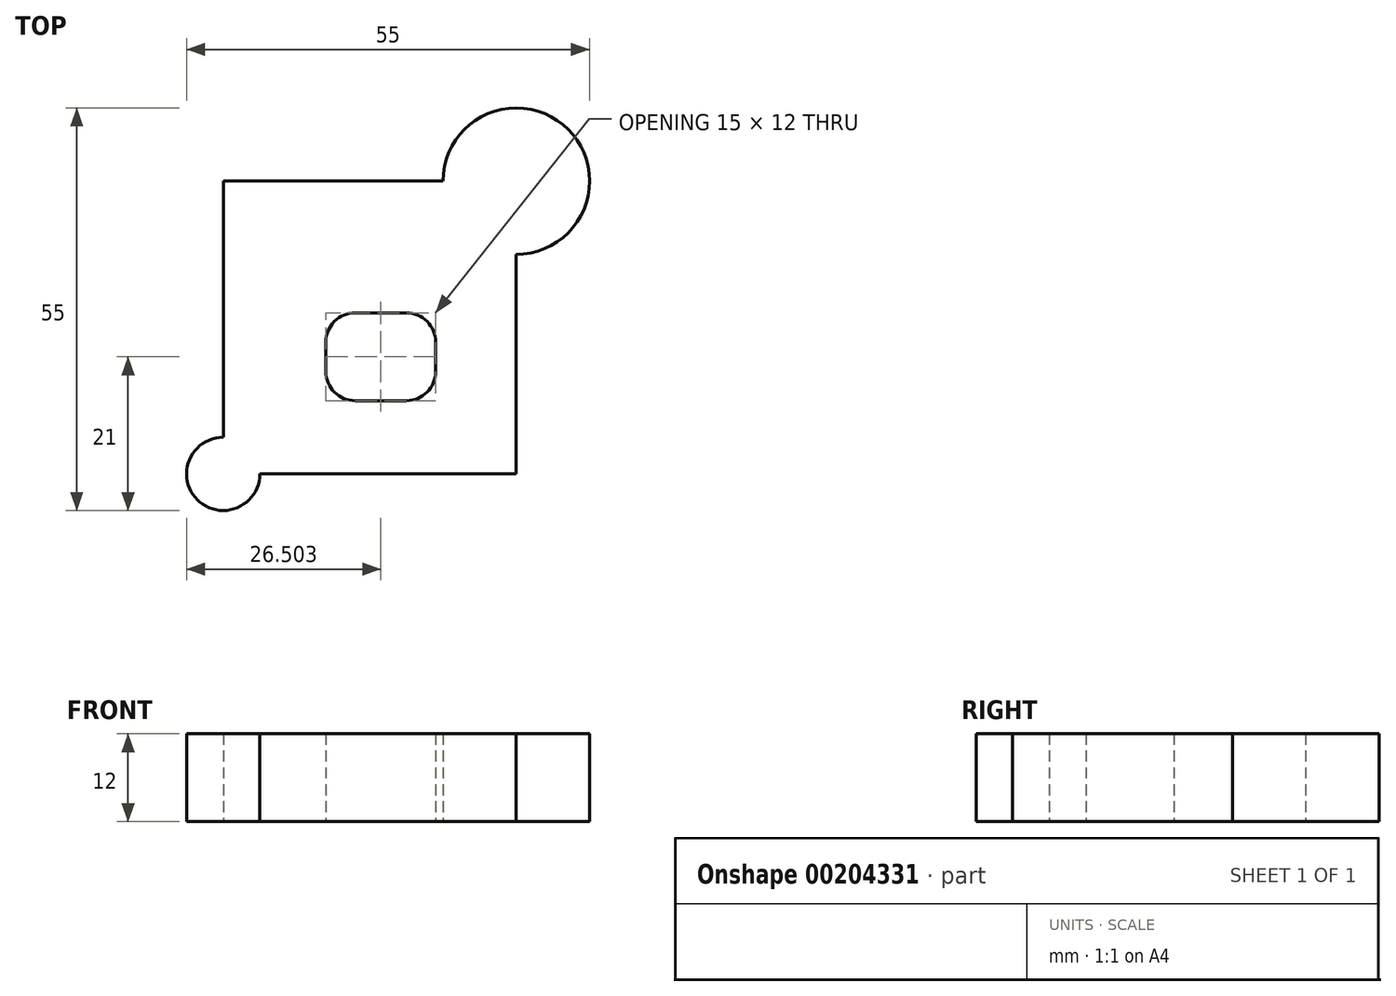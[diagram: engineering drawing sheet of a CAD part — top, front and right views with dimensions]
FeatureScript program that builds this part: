
annotation { "Feature Type Name" : "Feature", "Feature Type Description" : "" }
export const myFeature = defineFeature(function(context is Context, id is Id, definition is map)
    precondition{}
    {
        {
            var Q0;
            Q0=qCreatedBy(makeId("Top.planeOp"),FACE);
            var sketch = newSketch(context, id + "F0", { "sketchPlane" : qUnion([Q0])});
            skLineSegment(sketch, "E0.bottom", {"start": v(-39.87, 40) * mm, "end": v(0.13, 40) * mm});
            skLineSegment(sketch, "E0.top", {"start": v(-39.87, 0) * mm, "end": v(0.13, 0) * mm});
            skLineSegment(sketch, "E0.left", {"start": v(-39.87, 40) * mm, "end": v(-39.87, 0) * mm});
            skLineSegment(sketch, "E0.right", {"start": v(0.13, 40) * mm, "end": v(0.13, 0) * mm});
            skCircle(sketch, "E1", {"center": v(0.13, 40) * mm, "radius": 10 * mm});
            skCircle(sketch, "E2", {"center": v(-39.87, 0) * mm, "radius": 5 * mm});
            skLineSegment(sketch, "E3.bottom", {"start": v(-21.87, 22) * mm, "end": v(-14.87, 22) * mm});
            skLineSegment(sketch, "E3.top", {"start": v(-21.87, 10) * mm, "end": v(-14.87, 10) * mm});
            skLineSegment(sketch, "E3.left", {"start": v(-25.87, 18) * mm, "end": v(-25.87, 14) * mm});
            skLineSegment(sketch, "E3.right", {"start": v(-10.87, 18) * mm, "end": v(-10.87, 14) * mm});
            skPoint(sketch, "E4.visualSharp", {"position": v(-25.87, 22) * mm});
            skArc(sketch, "E4.filletArc", {"start": v(-21.87, 22) * mm, "mid": v(-24.7, 20.83) * mm, "end": v(-25.87, 18) * mm});
            skPoint(sketch, "E5.visualSharp", {"position": v(-10.87, 22) * mm});
            skArc(sketch, "E5.filletArc", {"start": v(-10.87, 18) * mm, "mid": v(-12.04, 20.83) * mm, "end": v(-14.87, 22) * mm});
            skPoint(sketch, "E6.visualSharp", {"position": v(-10.87, 10) * mm});
            skArc(sketch, "E6.filletArc", {"start": v(-14.87, 10) * mm, "mid": v(-12.04, 11.17) * mm, "end": v(-10.87, 14) * mm});
            skPoint(sketch, "E7.visualSharp", {"position": v(-25.87, 10) * mm});
            skArc(sketch, "E7.filletArc", {"start": v(-25.87, 14) * mm, "mid": v(-24.7, 11.17) * mm, "end": v(-21.87, 10) * mm});
            skSolve(sketch);
        }
        {
            var Q0;
            Q0=makeQuery(id+"F0.imprint","IMPRINT",FACE,{"disambiguationData":[TD([[makeQuery(id+"F0.imprint","IMPRINT",EDGE,{"derivedFrom":sQuery(id+"F0.wireOp",EDGE,"E3.bottom")}),1.0]])]});
            var Q1;
            {var subQ0=sQuery(id+"F0.wireOp",EDGE,"E0.right");var subQ1=sQuery(id+"F0.wireOp",EDGE,"E0.bottom");var subQ2=makeQuery(id+"F0.imprint","INTERSECT",VERTEX,{"derivedFrom":[subQ1,subQ0]});Q1=makeQuery(id+"F0.imprint","IMPRINT",FACE,{"disambiguationData":[TD([[makeQuery(id+"F0.imprint","IMPRINT",EDGE,{"disambiguationData":[TD([[subQ2,1.0]])],"derivedFrom":subQ1}),-1.0]])]});}
            var Q2;
            {var subQ0=sQuery(id+"F0.wireOp",EDGE,"E0.right");var subQ1=sQuery(id+"F0.wireOp",EDGE,"E0.bottom");var subQ2=makeQuery(id+"F0.imprint","INTERSECT",VERTEX,{"derivedFrom":[subQ1,subQ0]});Q2=makeQuery(id+"F0.imprint","IMPRINT",FACE,{"disambiguationData":[TD([[makeQuery(id+"F0.imprint","IMPRINT",EDGE,{"disambiguationData":[TD([[subQ2,1.0]])],"derivedFrom":subQ1}),1.0]])]});}
            var Q3;
            {var subQ0=sQuery(id+"F0.wireOp",EDGE,"E0.left");var subQ1=sQuery(id+"F0.wireOp",EDGE,"E0.top");var subQ2=makeQuery(id+"F0.imprint","INTERSECT",VERTEX,{"derivedFrom":[subQ1,subQ0]});Q3=makeQuery(id+"F0.imprint","IMPRINT",FACE,{"disambiguationData":[TD([[makeQuery(id+"F0.imprint","IMPRINT",EDGE,{"disambiguationData":[TD([[subQ2,-1.0]])],"derivedFrom":subQ1}),-1.0]])]});}
            var Q4;
            {var subQ0=sQuery(id+"F0.wireOp",EDGE,"E0.left");var subQ1=sQuery(id+"F0.wireOp",EDGE,"E0.top");var subQ2=makeQuery(id+"F0.imprint","INTERSECT",VERTEX,{"derivedFrom":[subQ1,subQ0]});Q4=makeQuery(id+"F0.imprint","IMPRINT",FACE,{"disambiguationData":[TD([[makeQuery(id+"F0.imprint","IMPRINT",EDGE,{"disambiguationData":[TD([[subQ2,-1.0]])],"derivedFrom":subQ1}),1.0]])]});}
            extrude(context, id + "F1", {"entities" : qUnion([Q0, Q1, Q2, Q3, Q4]), "depth" : 12 * mm});
        }
    });
